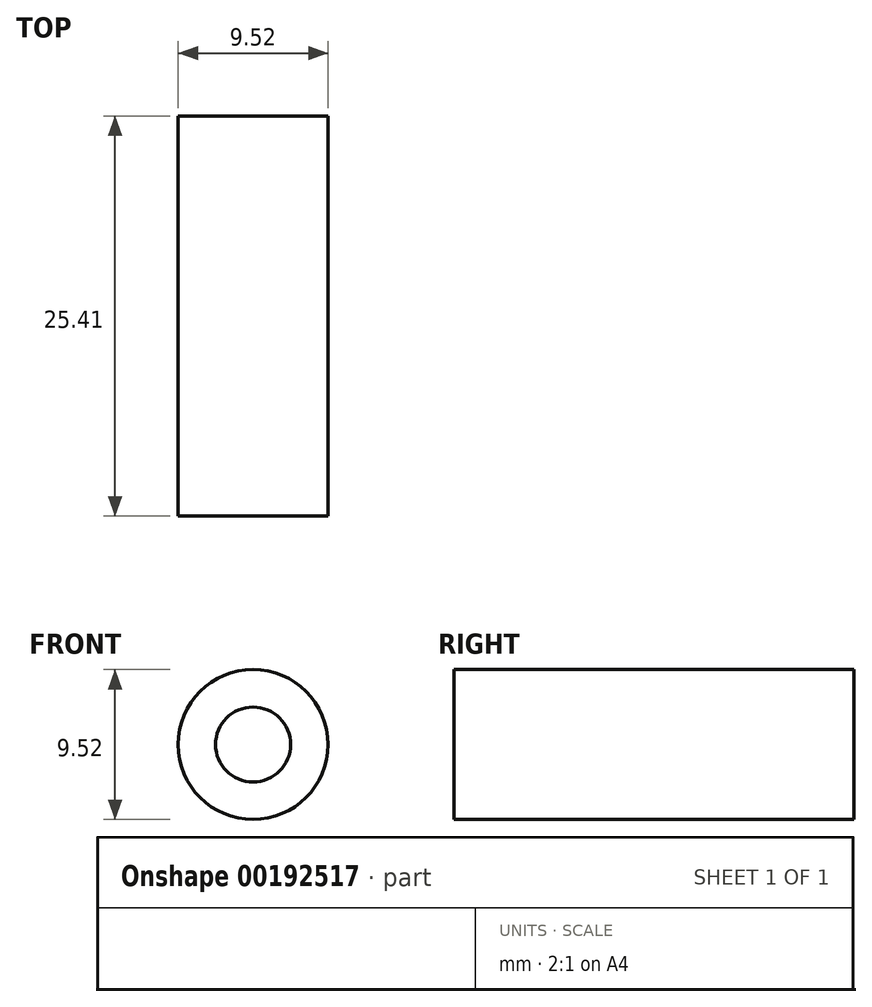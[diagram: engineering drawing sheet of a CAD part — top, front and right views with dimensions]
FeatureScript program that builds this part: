
annotation { "Feature Type Name" : "Feature", "Feature Type Description" : "" }
export const myFeature = defineFeature(function(context is Context, id is Id, definition is map)
    precondition{}
    {
        {
            var Q0;
            Q0=qCreatedBy(makeId("Front.planeOp"),FACE);
            var sketch = newSketch(context, id + "F0", { "sketchPlane" : qUnion([Q0])});
            skCircle(sketch, "E0", {"center": v(0, 0) * mm, "radius": 4.76 * mm});
            skSolve(sketch);
        }
        {
            var Q0;
            Q0 = qSketchRegion(id + "F0", true);
            extrude(context, id + "F1", {"entities" : qUnion([Q0]), "depth" : 25.4 * mm});
        }
        {
            var Q0;
            Q0=makeQuery(id+"F1.opExtrude","CAP_FACE",FACE,{"disambiguationData":[OSD([sQuery(id+"F0.wireOp",EDGE,"E0")])],"isStart":false});
            var sketch = newSketch(context, id + "F2", { "sketchPlane" : qUnion([Q0])});
            skCircle(sketch, "E1", {"center": v(0, 0) * mm, "radius": 2.38 * mm});
            skSolve(sketch);
        }
        {
            var Q0;
            Q0=makeQuery(id+"F2.imprint","IMPRINT",FACE,{"disambiguationData":[TD([[makeQuery(id+"F2.imprint","IMPRINT",EDGE,{"derivedFrom":sQuery(id+"F2.wireOp",EDGE,"E1")}),1.0]])]});
            extrude(context, id + "F3", {"entities" : qUnion([Q0]), "operationType" : NewBodyOperationType.ADD, "depth" : 3 / 203.2 * mm});
        }
    });
